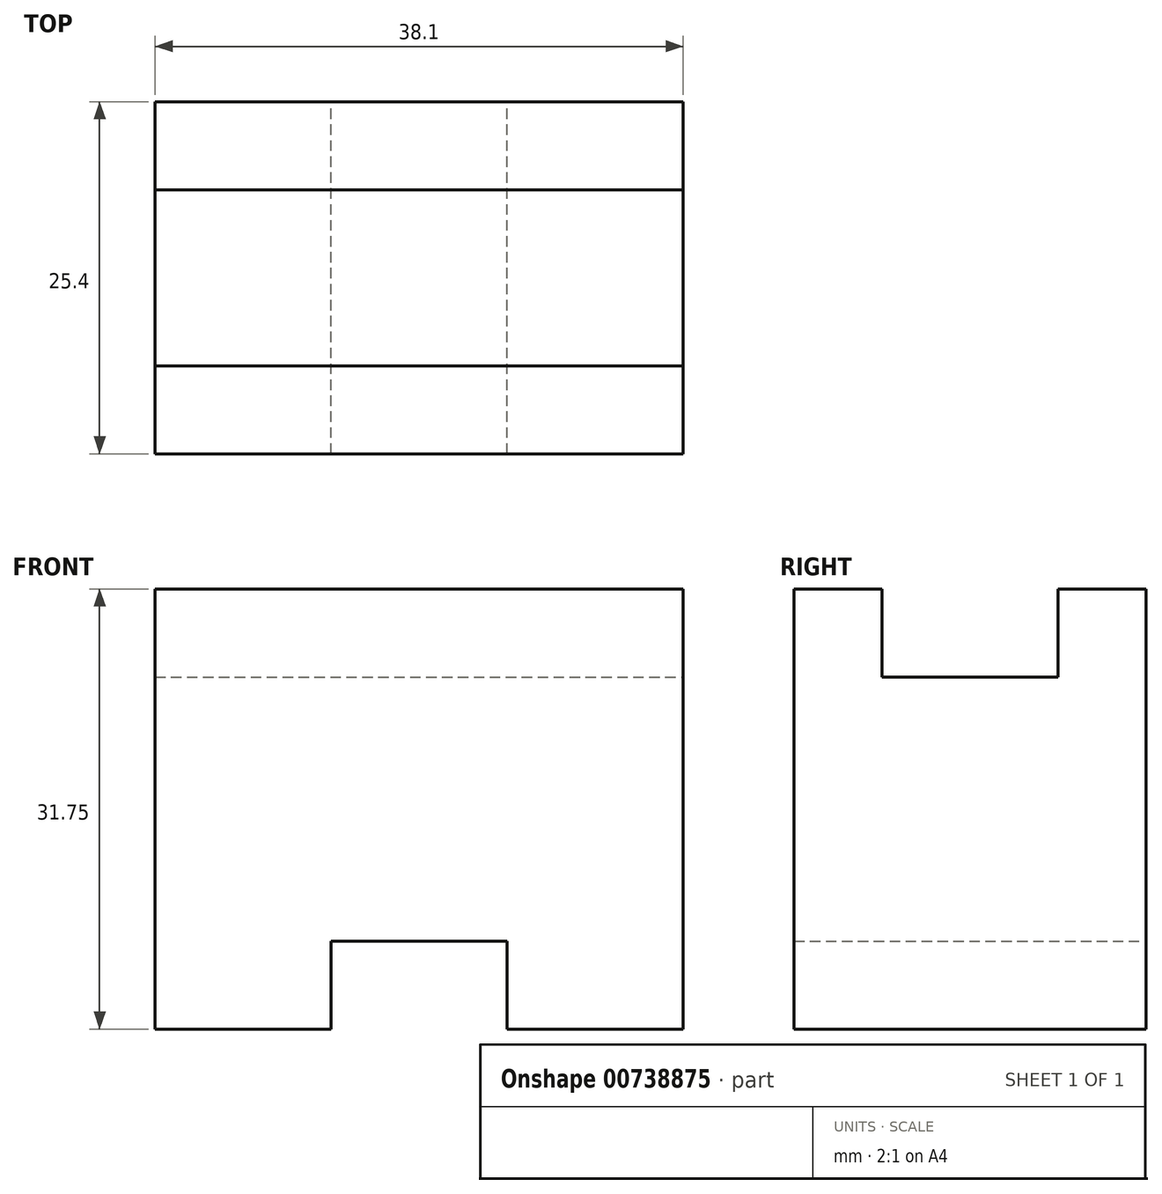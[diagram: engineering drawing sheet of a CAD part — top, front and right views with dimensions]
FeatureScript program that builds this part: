
annotation { "Feature Type Name" : "Feature", "Feature Type Description" : "" }
export const myFeature = defineFeature(function(context is Context, id is Id, definition is map)
    precondition{}
    {
        {
            var Q0;
            Q0=qCreatedBy(makeId("Front.planeOp"),FACE);
            var sketch = newSketch(context, id + "F0", { "sketchPlane" : qUnion([Q0])});
            skLineSegment(sketch, "E0", {"start": v(0, 31.75) * mm, "end": v(0, 0) * mm});
            skLineSegment(sketch, "E1", {"start": v(0, 31.75) * mm, "end": v(38.1, 31.75) * mm});
            skLineSegment(sketch, "E2", {"start": v(38.1, 31.75) * mm, "end": v(38.1, 0) * mm});
            skLineSegment(sketch, "E3", {"start": v(0, 0) * mm, "end": v(38.1, 0) * mm});
            skSolve(sketch);
        }
        {
            var Q0;
            Q0 = qSketchRegion(id + "F0", true);
            extrude(context, id + "F1", {"entities" : qUnion([Q0]), "depth" : 25.4 * mm, "offsetDistance" : 25.4 * mm});
        }
        {
            var Q0;
            Q0=makeQuery(id+"F1.opExtrude","SWEPT_FACE",FACE,{"disambiguationData":[OSD([sQuery(id+"F0.wireOp",EDGE,"E1")])]});
            var sketch = newSketch(context, id + "F2", { "sketchPlane" : qUnion([Q0])});
            skLineSegment(sketch, "E4", {"start": v(0, -6.35) * mm, "end": v(38.1, -6.35) * mm});
            skLineSegment(sketch, "E5", {"start": v(0, -19.05) * mm, "end": v(38.1, -19.05) * mm});
            skSolve(sketch);
        }
        {
            var Q0;
            Q0 = qSketchRegion(id + "F2", true);
            var Q1;
            {var subQ0=sQuery(id+"F2.wireOp",EDGE,"E4");Q1=makeQuery(id+"F2.imprint","IMPRINT",FACE,{"disambiguationData":[TD([[makeQuery(id+"F2.imprint","IMPRINT",EDGE,{"derivedFrom":subQ0}),-1.0]])]});}
            extrude(context, id + "F3", {"entities" : qUnion([Q0, Q1]), "operationType" : NewBodyOperationType.REMOVE, "oppositeDirection" : true, "depth" : 6.35 * mm, "offsetDistance" : 25.4 * mm});
        }
        {
            var Q0;
            Q0=makeQuery(id+"F1.opExtrude","SWEPT_FACE",FACE,{"disambiguationData":[OSD([sQuery(id+"F0.wireOp",EDGE,"E3")])]});
            var sketch = newSketch(context, id + "F4", { "sketchPlane" : qUnion([Q0])});
            skLineSegment(sketch, "E6", {"start": v(12.7, 25.4) * mm, "end": v(12.7, 0) * mm});
            skLineSegment(sketch, "E7", {"start": v(25.4, 25.4) * mm, "end": v(25.4, 0) * mm});
            skLineSegment(sketch, "E8", {"start": v(12.7, 21.11) * mm, "end": v(25.4, 21.11) * mm});
            skSolve(sketch);
        }
        {
            var Q0;
            Q0 = qSketchRegion(id + "F4", true);
            var Q1;
            {var subQ0=sQuery(id+"F4.wireOp",EDGE,"E6");Q1=makeQuery(id+"F4.imprint","IMPRINT",FACE,{"disambiguationData":[TD([[makeQuery(id+"F4.imprint","IMPRINT",EDGE,{"derivedFrom":subQ0}),1.0]])]});}
            extrude(context, id + "F5", {"entities" : qUnion([Q0, Q1]), "operationType" : NewBodyOperationType.REMOVE, "oppositeDirection" : true, "depth" : 6.35 * mm, "offsetDistance" : 25.4 * mm});
        }
    });
